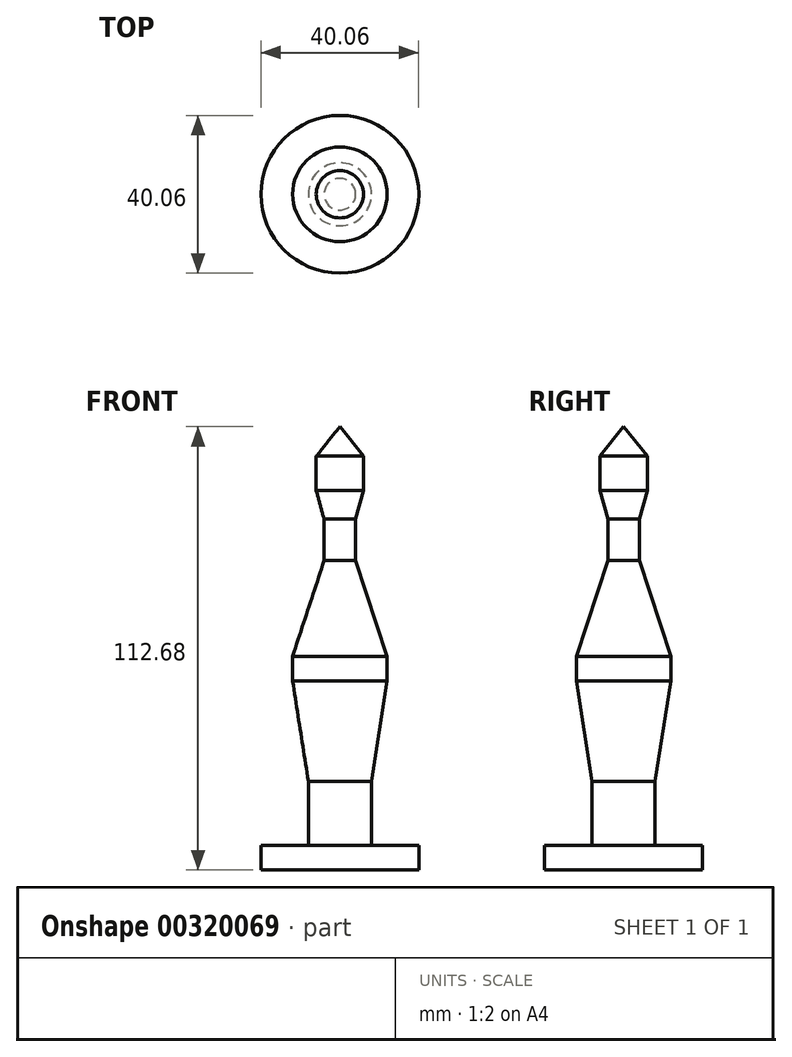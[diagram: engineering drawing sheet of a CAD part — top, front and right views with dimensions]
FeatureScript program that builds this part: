
annotation { "Feature Type Name" : "Feature", "Feature Type Description" : "" }
export const myFeature = defineFeature(function(context is Context, id is Id, definition is map)
    precondition{}
    {
        {
            var Q0;
            Q0=qCreatedBy(makeId("Front.planeOp"),FACE);
            var sketch = newSketch(context, id + "F0", { "sketchPlane" : qUnion([Q0])});
            skLineSegment(sketch, "E0", {"start": v(0, 67.73) * mm, "end": v(-6, 60.22) * mm});
            skLineSegment(sketch, "E1", {"start": v(-6, 60.22) * mm, "end": v(-6, 51.46) * mm});
            skLineSegment(sketch, "E2", {"start": v(-6, 51.46) * mm, "end": v(-4, 44.2) * mm});
            skLineSegment(sketch, "E3", {"start": v(-4, 44.2) * mm, "end": v(-4, 33.68) * mm});
            skLineSegment(sketch, "E4", {"start": v(-4, 33.68) * mm, "end": v(-12.02, 9.39) * mm});
            skLineSegment(sketch, "E5", {"start": v(-12.02, 9.39) * mm, "end": v(-12.02, 3.13) * mm});
            skLineSegment(sketch, "E6", {"start": v(-12.02, 3.13) * mm, "end": v(-8.01, -22.41) * mm});
            skLineSegment(sketch, "E7", {"start": v(-8.01, -22.41) * mm, "end": v(-8.01, -38.69) * mm});
            skLineSegment(sketch, "E8", {"start": v(-8.01, -38.69) * mm, "end": v(-20.03, -38.69) * mm});
            skLineSegment(sketch, "E9", {"start": v(-20.03, -38.69) * mm, "end": v(-20.03, -44.95) * mm});
            skLineSegment(sketch, "E10", {"start": v(-20.03, -44.95) * mm, "end": v(0, -44.95) * mm});
            skLineSegment(sketch, "E11", {"start": v(0, -44.95) * mm, "end": v(0, 67.73) * mm});
            skSolve(sketch);
        }
        {
            var Q0;
            Q0=makeQuery(id+"F0.imprint","IMPRINT",FACE,{"disambiguationData":[TD([[makeQuery(id+"F0.imprint","IMPRINT",EDGE,{"derivedFrom":sQuery(id+"F0.wireOp",EDGE,"E0")}),1.0]])]});
            var Q1;
            Q1=sQuery(id+"F0.wireOp",EDGE,"E11");
            revolve(context, id + "F1", {"entities" : qUnion([Q0]), "axis" : qUnion([Q1]), "revolveType" : RevolveType.FULL});
        }
    });
